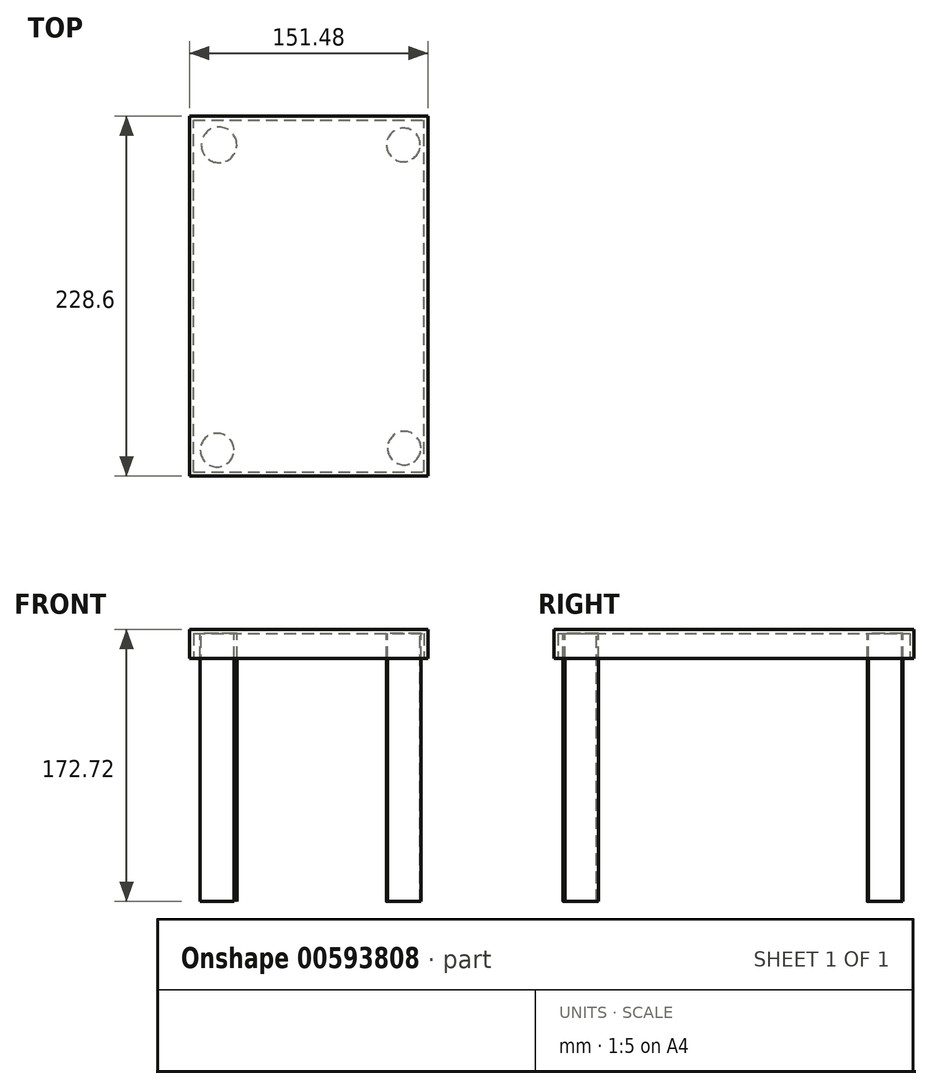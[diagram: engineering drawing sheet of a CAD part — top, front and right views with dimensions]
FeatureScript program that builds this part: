
annotation { "Feature Type Name" : "Feature", "Feature Type Description" : "" }
export const myFeature = defineFeature(function(context is Context, id is Id, definition is map)
    precondition{}
    {
        {
            var Q0;
            Q0=qCreatedBy(makeId("Front.planeOp"),FACE);
            var sketch = newSketch(context, id + "F0", { "sketchPlane" : qUnion([Q0])});
            skLineSegment(sketch, "E0.bottom", {"start": v(-75.74, 18.29) * mm, "end": v(75.74, 18.29) * mm});
            skLineSegment(sketch, "E0.top", {"start": v(-75.74, 0) * mm, "end": v(75.74, 0) * mm});
            skLineSegment(sketch, "E0.left", {"start": v(-75.74, 18.29) * mm, "end": v(-75.74, 0) * mm});
            skLineSegment(sketch, "E0.right", {"start": v(75.74, 18.29) * mm, "end": v(75.74, 0) * mm});
            skSolve(sketch);
        }
        {
            var Q0;
            Q0=makeQuery(id+"F0.imprint","IMPRINT",FACE,{"disambiguationData":[TD([[makeQuery(id+"F0.imprint","IMPRINT",EDGE,{"derivedFrom":sQuery(id+"F0.wireOp",EDGE,"E0.bottom")}),-1.0]])]});
            extrude(context, id + "F1", {"entities" : qUnion([Q0]), "depth" : 228.6 * mm, "offsetDistance" : 25.4 * mm});
        }
        {
            var Q0;
            Q0=makeQuery(id+"F1.opExtrude","SWEPT_FACE",FACE,{"disambiguationData":[OSD([sQuery(id+"F0.wireOp",EDGE,"E0.top")])]});
            shell(context, id + "F2", {"entities" : qUnion([Q0]), "thickness" : 2.54 * mm});
        }
        {
            var Q0;
            Q0=makeQuery(id+"F2.opShell","OFFSET_FACE",FACE,{"disambiguationData":[OSD([sQuery(id+"F0.wireOp",EDGE,"E0.bottom")])]});
            var sketch = newSketch(context, id + "F3", { "sketchPlane" : qUnion([Q0])});
            skCircle(sketch, "E1", {"center": v(-58.22, 212.14) * mm, "radius": 10.68 * mm});
            skCircle(sketch, "E2", {"center": v(-57, 18.29) * mm, "radius": 11.29 * mm});
            skCircle(sketch, "E3", {"center": v(60.05, 18.29) * mm, "radius": 10.7 * mm});
            skCircle(sketch, "E4", {"center": v(60.66, 210.92) * mm, "radius": 10.66 * mm});
            skSolve(sketch);
        }
        {
            var Q0;
            Q0=sQuery(id+"F3.wireOp",EDGE,"E1");
            extrude(context, id + "F4", {"bodyType" : ToolBodyType.SURFACE, "surfaceEntities" : qUnion([Q0]), "depth" : 165.1 * mm, "offsetDistance" : 25.4 * mm});
        }
        {
            var Q0;
            Q0=sQuery(id+"F3.wireOp",EDGE,"E2");
            extrude(context, id + "F5", {"bodyType" : ToolBodyType.SURFACE, "surfaceEntities" : qUnion([Q0]), "depth" : 165.1 * mm, "offsetDistance" : 25.4 * mm});
        }
        {
            var Q0;
            Q0=sQuery(id+"F3.wireOp",EDGE,"E3");
            extrude(context, id + "F6", {"bodyType" : ToolBodyType.SURFACE, "surfaceEntities" : qUnion([Q0]), "depth" : 165.1 * mm, "offsetDistance" : 25.4 * mm});
        }
        {
            var Q0;
            Q0=sQuery(id+"F3.wireOp",EDGE,"E4");
            extrude(context, id + "F7", {"bodyType" : ToolBodyType.SURFACE, "surfaceEntities" : qUnion([Q0]), "depth" : 165.1 * mm, "offsetDistance" : 25.4 * mm});
        }
        {
            var Q0;
            Q0 = qSketchRegion(id + "F3", true);
            extrude(context, id + "F8", {"entities" : qUnion([Q0]), "operationType" : NewBodyOperationType.ADD, "depth" : 170.18 * mm, "offsetDistance" : 25.4 * mm});
        }
    });
